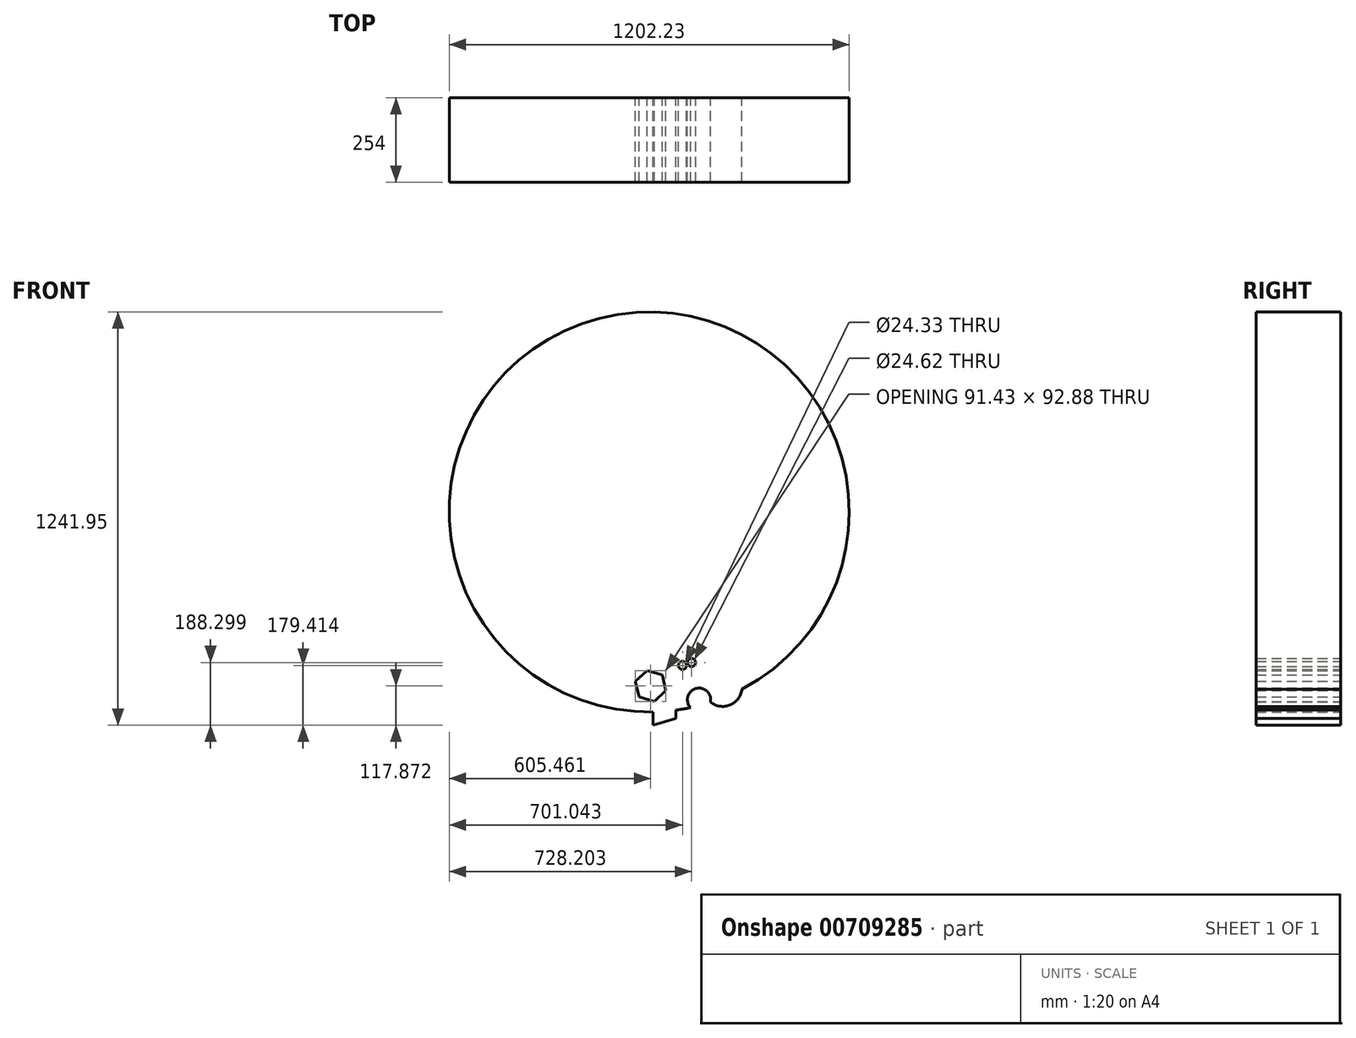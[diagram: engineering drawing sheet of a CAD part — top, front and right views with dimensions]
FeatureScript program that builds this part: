
annotation { "Feature Type Name" : "Feature", "Feature Type Description" : "" }
export const myFeature = defineFeature(function(context is Context, id is Id, definition is map)
    precondition{}
    {
        {
            var Q0;
            Q0=qCreatedBy(makeId("Front.planeOp"),FACE);
            var sketch = newSketch(context, id + "F0", { "sketchPlane" : qUnion([Q0])});
            skLineSegment(sketch, "E0", {"start": v(-248.36, -79.8) * mm, "end": v(-248.36, -167.39) * mm});
            skLineSegment(sketch, "E1", {"start": v(-248.36, -167.39) * mm, "end": v(-179.41, -147.11) * mm});
            skLineSegment(sketch, "E2", {"start": v(-179.41, -147.11) * mm, "end": v(-179.41, -58.18) * mm});
            skLineSegment(sketch, "E3", {"start": v(-179.41, -58.18) * mm, "end": v(-248.36, -79.8) * mm});
            skCircle(sketch, "E4.cCircle", {"center": v(-255.67, -49.52) * mm, "radius": 41.33 * mm, "construction": true});
            skLineSegment(sketch, "E4.0", {"start": v(-220.95, -16.78) * mm, "end": v(-209.95, -63.22) * mm});
            skLineSegment(sketch, "E4.1", {"start": v(-209.95, -63.22) * mm, "end": v(-244.68, -95.96) * mm});
            skLineSegment(sketch, "E4.2", {"start": v(-244.68, -95.96) * mm, "end": v(-290.39, -82.26) * mm});
            skLineSegment(sketch, "E4.3", {"start": v(-290.39, -82.26) * mm, "end": v(-301.38, -35.82) * mm});
            skLineSegment(sketch, "E4.4", {"start": v(-301.38, -35.82) * mm, "end": v(-266.66, -3.08) * mm});
            skLineSegment(sketch, "E4.5", {"start": v(-266.66, -3.08) * mm, "end": v(-220.95, -16.78) * mm});
            skPoint(sketch, "E4.0.midPoint", {"position": v(-215.45, -40) * mm});
            skCircle(sketch, "E5", {"center": v(-160.09, 12.02) * mm, "radius": 12.17 * mm});
            skCircle(sketch, "E6", {"center": v(-132.93, 20.9) * mm, "radius": 12.3 * mm});
            skLineSegment(sketch, "E7", {"start": v(-180.98, -22.73) * mm, "end": v(-155.39, -22.73) * mm});
            skLineSegment(sketch, "E8", {"start": v(-155.39, -22.14) * mm, "end": v(-133.97, -13.34) * mm});
            skLineSegment(sketch, "E9", {"start": v(-133.97, -13.34) * mm, "end": v(-119.35, 4.98) * mm});
            skPoint(sketch, "E10", {"position": v(-97.41, 52.05) * mm});
            skPoint(sketch, "E11", {"position": v(-119.35, -3.9) * mm});
            skPoint(sketch, "E12", {"position": v(-95.32, 31.24) * mm});
            skPoint(sketch, "E13", {"position": v(-127.18, 46.07) * mm});
            skPoint(sketch, "E14", {"position": v(-98.98, 41.68) * mm});
            skPoint(sketch, "E15", {"position": v(-108.9, 75.37) * mm});
            skPoint(sketch, "E16", {"position": v(-116.74, 40.2) * mm});
            skPoint(sketch, "E17", {"position": v(-80.7, 75.16) * mm});
            skPoint(sketch, "E18", {"position": v(-133.45, 52.05) * mm});
            skPoint(sketch, "E19", {"position": v(-103.16, 63.98) * mm});
            skPoint(sketch, "E20", {"position": v(-88.53, 98.5) * mm});
            skArc(sketch, "E21", {"start": v(-76, -97.93) * mm, "mid": v(6.37, -17.16) * mm, "end": v(-91.14, -78.8) * mm});
            skArc(sketch, "E22", {"start": v(-76, -97.93) * mm, "mid": v(-119.76, -57.28) * mm, "end": v(-136.06, -114.75) * mm});
            skArc(sketch, "E23", {"start": v(-128.75, -113.16) * mm, "mid": v(-387.63, 1060.86) * mm, "end": v(-136.06, -114.75) * mm});
            skSolve(sketch);
        }
        {
            var Q0;
            Q0 = qSketchRegion(id + "F0", true);
            extrude(context, id + "F1", {"entities" : qUnion([Q0]), "depth" : 254 * mm, "offsetDistance" : 25.4 * mm});
        }
    });
